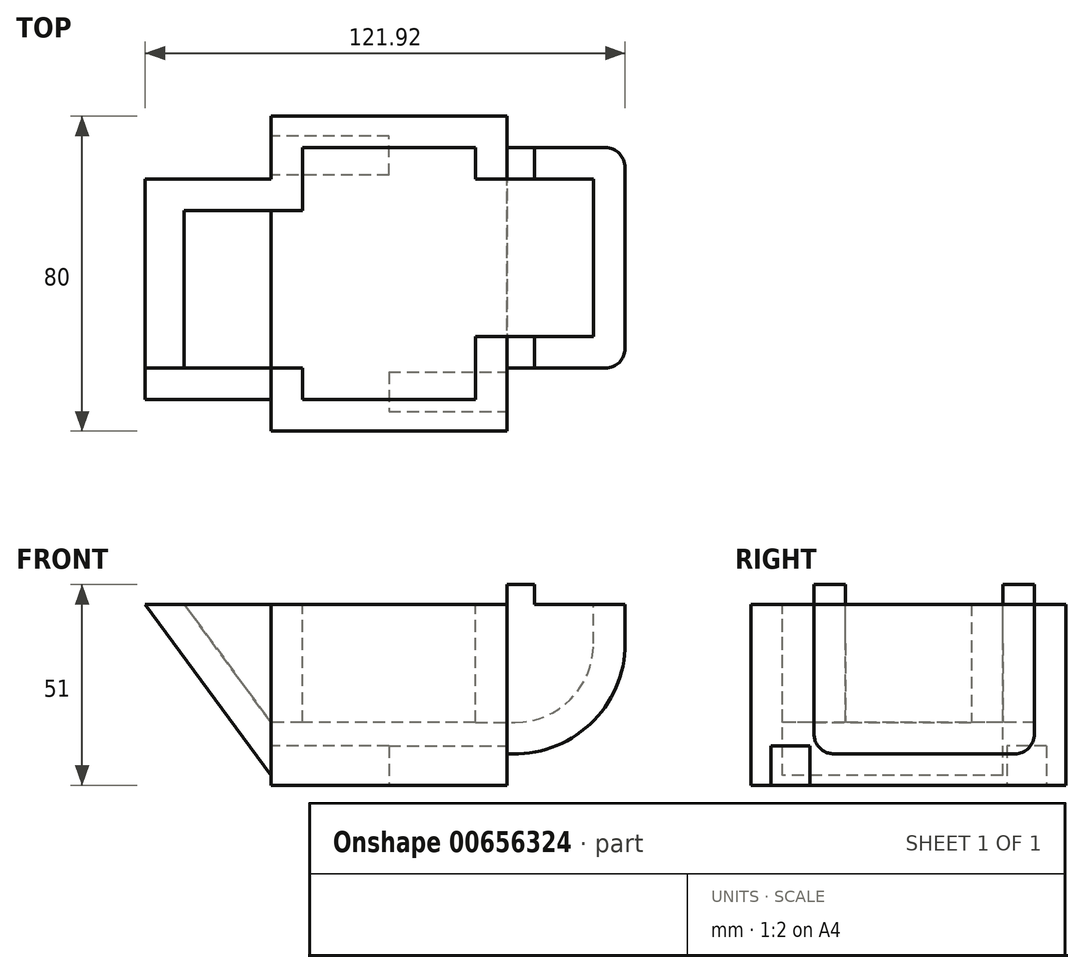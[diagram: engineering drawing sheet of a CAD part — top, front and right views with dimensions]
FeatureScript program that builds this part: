
annotation { "Feature Type Name" : "Feature", "Feature Type Description" : "" }
export const myFeature = defineFeature(function(context is Context, id is Id, definition is map)
    precondition{}
    {
        {
            var Q0;
            Q0=qCreatedBy(makeId("Top.planeOp"),FACE);
            var sketch = newSketch(context, id + "F0", { "sketchPlane" : qUnion([Q0])});
            skLineSegment(sketch, "E0.bottom", {"start": v(30, 40) * mm, "end": v(-30, 40) * mm});
            skLineSegment(sketch, "E0.top", {"start": v(30, -40) * mm, "end": v(-30, -40) * mm});
            skLineSegment(sketch, "E0.left", {"start": v(30, 40) * mm, "end": v(30, -40) * mm});
            skLineSegment(sketch, "E0.right", {"start": v(-30, 40) * mm, "end": v(-30, -40) * mm});
            skPoint(sketch, "E0.middle", {"position": v(0, 0) * mm});
            skSolve(sketch);
        }
        {
            var Q0;
            Q0=makeQuery(id+"F0.imprint","IMPRINT",FACE,{"disambiguationData":[TD([[makeQuery(id+"F0.imprint","IMPRINT",EDGE,{"derivedFrom":sQuery(id+"F0.wireOp",EDGE,"E0.bottom")}),1.0]])]});
            var sketch = newSketch(context, id + "F1", { "sketchPlane" : qUnion([Q0])});
            skCircle(sketch, "E1", {"center": v(0, 0) * mm, "radius": 25 * mm});
            skLineSegment(sketch, "E2.bottom", {"start": v(0, 25) * mm, "end": v(30, 25) * mm});
            skLineSegment(sketch, "E2.top", {"start": v(0, 35) * mm, "end": v(30, 35) * mm});
            skLineSegment(sketch, "E2.left", {"start": v(0, 25) * mm, "end": v(0, 35) * mm});
            skLineSegment(sketch, "E2.right", {"start": v(30, 25) * mm, "end": v(30, 35) * mm});
            skLineSegment(sketch, "E3.bottom", {"start": v(0, 25) * mm, "end": v(-30, 25) * mm});
            skLineSegment(sketch, "E3.top", {"start": v(0, 35) * mm, "end": v(-30, 35) * mm});
            skLineSegment(sketch, "E3.right", {"start": v(-30, 25) * mm, "end": v(-30, 35) * mm});
            skLineSegment(sketch, "E4.MirrorCS", {"start": v(0, -25) * mm, "end": v(30, -25) * mm});
            skLineSegment(sketch, "E5.MirrorCS", {"start": v(30, -25) * mm, "end": v(30, -35) * mm});
            skLineSegment(sketch, "E6.MirrorCS", {"start": v(0, -35) * mm, "end": v(30, -35) * mm});
            skLineSegment(sketch, "E7.MirrorCS", {"start": v(0, -35) * mm, "end": v(-30, -35) * mm});
            skLineSegment(sketch, "E8.MirrorCS", {"start": v(0, -25) * mm, "end": v(-30, -25) * mm});
            skLineSegment(sketch, "E9.MirrorCS", {"start": v(-30, -25) * mm, "end": v(-30, -35) * mm});
            skLineSegment(sketch, "E10", {"start": v(0, -25) * mm, "end": v(0, -35) * mm});
            skSolve(sketch);
        }
        {
            var Q0;
            Q0 = qSketchRegion(id + "F0", true);
            extrude(context, id + "F2", {"entities" : qUnion([Q0]), "depth" : 46 * mm, "offsetDistance" : 25 * mm});
        }
        {
            var Q0;
            Q0=makeQuery(id+"F1.imprint","IMPRINT",FACE,{"disambiguationData":[TD([[makeQuery(id+"F1.imprint","IMPRINT",EDGE,{"derivedFrom":sQuery(id+"F1.wireOp",EDGE,"E3.bottom")}),-1.0]])]});
            var Q1;
            Q1=makeQuery(id+"F1.imprint","IMPRINT",FACE,{"disambiguationData":[TD([[makeQuery(id+"F1.imprint","IMPRINT",EDGE,{"derivedFrom":sQuery(id+"F1.wireOp",EDGE,"E4.MirrorCS")}),-1.0]])]});
            var Q2;
            Q2=makeQuery(id+"F1.imprint","IMPRINT",FACE,{"disambiguationData":[TD([[makeQuery(id+"F1.imprint","IMPRINT",EDGE,{"derivedFrom":sQuery(id+"F1.wireOp",EDGE,"E4.MirrorCS")}),-1.0]])]});
            extrude(context, id + "F3", {"entities" : qUnion([Q0, Q1, Q2]), "operationType" : NewBodyOperationType.REMOVE, "depth" : 10 * mm, "offsetDistance" : 25 * mm});
        }
        {
            var Q0;
            Q0=makeQuery(id+"F2.opExtrude","CAP_FACE",FACE,{"disambiguationData":[OSD([sQuery(id+"F0.wireOp",EDGE,"E0.bottom"),sQuery(id+"F0.wireOp",EDGE,"E0.top"),sQuery(id+"F0.wireOp",EDGE,"E0.left"),sQuery(id+"F0.wireOp",EDGE,"E0.right")])],"isStart":false});
            var sketch = newSketch(context, id + "F4", { "sketchPlane" : qUnion([Q0])});
            skLineSegment(sketch, "E11.bottom", {"start": v(22, 32) * mm, "end": v(-22, 32) * mm});
            skLineSegment(sketch, "E11.top", {"start": v(22, -32) * mm, "end": v(-22, -32) * mm});
            skLineSegment(sketch, "E11.left", {"start": v(22, 32) * mm, "end": v(22, -32) * mm});
            skLineSegment(sketch, "E11.right", {"start": v(-22, 32) * mm, "end": v(-22, -32) * mm});
            skPoint(sketch, "E11.middle", {"position": v(0, 0) * mm});
            skSolve(sketch);
        }
        {
            var Q0;
            Q0=makeQuery(id+"F4.imprint","IMPRINT",FACE,{"disambiguationData":[TD([[makeQuery(id+"F4.imprint","IMPRINT",EDGE,{"derivedFrom":sQuery(id+"F4.wireOp",EDGE,"E11.bottom")}),1.0]])]});
            extrude(context, id + "F5", {"entities" : qUnion([Q0]), "operationType" : NewBodyOperationType.REMOVE, "oppositeDirection" : true, "depth" : 30 * mm, "offsetDistance" : 25 * mm});
        }
        {
            var Q0;
            Q0=makeQuery(id+"F2.opExtrude","CAP_FACE",FACE,{"disambiguationData":[OSD([sQuery(id+"F0.wireOp",EDGE,"E0.bottom"),sQuery(id+"F0.wireOp",EDGE,"E0.top"),sQuery(id+"F0.wireOp",EDGE,"E0.left"),sQuery(id+"F0.wireOp",EDGE,"E0.right")])],"isStart":false});
            var sketch = newSketch(context, id + "F6", { "sketchPlane" : qUnion([Q0])});
            skLineSegment(sketch, "E12.bottom", {"start": v(30, 24) * mm, "end": v(-30, 24) * mm});
            skLineSegment(sketch, "E12.top", {"start": v(30, -24) * mm, "end": v(-30, -24) * mm});
            skLineSegment(sketch, "E12.left", {"start": v(30, 24) * mm, "end": v(30, -24) * mm});
            skLineSegment(sketch, "E12.right", {"start": v(-30, 24) * mm, "end": v(-30, -24) * mm});
            skPoint(sketch, "E12.middle", {"position": v(0, 0) * mm});
            skLineSegment(sketch, "E13.bottom", {"start": v(22, 24) * mm, "end": v(-22, 24) * mm});
            skLineSegment(sketch, "E13.top", {"start": v(22, -24) * mm, "end": v(-22, -24) * mm});
            skLineSegment(sketch, "E13.left", {"start": v(22, 24) * mm, "end": v(22, -24) * mm});
            skLineSegment(sketch, "E13.right", {"start": v(-22, 24) * mm, "end": v(-22, -24) * mm});
            skSolve(sketch);
        }
        {
            var Q0;
            {var subQ0=sQuery(id+"F6.wireOp",EDGE,"E12.right");Q0=makeQuery(id+"F6.imprint","IMPRINT",FACE,{"disambiguationData":[TD([[makeQuery(id+"F6.imprint","IMPRINT",EDGE,{"derivedFrom":subQ0}),1.0]])]});}
            var Q1;
            {var subQ0=sQuery(id+"F6.wireOp",EDGE,"E12.left");Q1=makeQuery(id+"F6.imprint","IMPRINT",FACE,{"disambiguationData":[TD([[makeQuery(id+"F6.imprint","IMPRINT",EDGE,{"derivedFrom":subQ0}),-1.0]])]});}
            var Q2;
            Q2=makeQuery(id+"F5.boolean.opBoolean","COPY",FACE,{"derivedFrom":makeQuery(id+"F5.opExtrude","CAP_FACE",FACE,{"disambiguationData":[OSD([sQuery(id+"F4.wireOp",EDGE,"E11.bottom"),sQuery(id+"F4.wireOp",EDGE,"E11.top"),sQuery(id+"F4.wireOp",EDGE,"E11.left"),sQuery(id+"F4.wireOp",EDGE,"E11.right")])],"isStart":false})});
            extrude(context, id + "F7", {"entities" : qUnion([Q0, Q1]), "operationType" : NewBodyOperationType.REMOVE, "endBound" : BoundingType.UP_TO_SURFACE, "oppositeDirection" : true, "depth" : 25 * mm, "endBoundEntityFace" : qUnion([Q2]), "offsetDistance" : 25 * mm});
        }
        {
            var Q0;
            {var subQ0=sQuery(id+"F6.wireOp",EDGE,"E12.top");Q0=makeQuery(id+"F7.boolean.opBoolean","COPY",FACE,{"derivedFrom":makeQuery(id+"F7.opExtrude","SWEPT_FACE",FACE,{"disambiguationData":[OSD([subQ0]),TDD([makeQuery(id+"F6.imprint","IMPRINT",EDGE,{"disambiguationData":[TD([[makeQuery(id+"F6.imprint","INTERSECT",VERTEX,{"derivedFrom":[makeQuery(id+"F2.opExtrude","CAP_EDGE",EDGE,{"disambiguationData":[OSD([sQuery(id+"F0.wireOp",EDGE,"E0.left")])],"isStart":false}),subQ0,sQuery(id+"F6.wireOp",EDGE,"E12.left")]}),-1.0]])],"derivedFrom":subQ0})])]})});}
            var sketch = newSketch(context, id + "F8", { "sketchPlane" : qUnion([Q0])});
            skLineSegment(sketch, "E14.bottom", {"start": v(-22, 16) * mm, "end": v(-52, 16) * mm});
            skLineSegment(sketch, "E14.top", {"start": v(-22, 46) * mm, "end": v(-52, 46) * mm});
            skLineSegment(sketch, "E14.left", {"start": v(-22, 16) * mm, "end": v(-22, 46) * mm});
            skLineSegment(sketch, "E14.right", {"start": v(-52, 16) * mm, "end": v(-52, 46) * mm});
            skSolve(sketch);
        }
        {
            var Q0;
            {var subQ2=sQuery(id+"F8.wireOp",EDGE,"E14.right");Q0=makeQuery(id+"F8.imprint","IMPRINT",FACE,{"disambiguationData":[TD([[makeQuery(id+"F8.imprint","IMPRINT",EDGE,{"derivedFrom":subQ2}),-1.0]])]});}
            var Q1;
            {var subQ2=sQuery(id+"F8.wireOp",EDGE,"E14.left");Q1=makeQuery(id+"F8.imprint","IMPRINT",FACE,{"disambiguationData":[TD([[makeQuery(id+"F8.imprint","IMPRINT",EDGE,{"derivedFrom":subQ2}),1.0]])]});}
            extrude(context, id + "F9", {"entities" : qUnion([Q0, Q1]), "operationType" : NewBodyOperationType.ADD, "depth" : 8 * mm, "offsetDistance" : 25 * mm});
        }
        {
            var Q0;
            Q0=makeQuery(id+"F9.opExtrude","SWEPT_EDGE",EDGE,{"disambiguationData":[OSD([sQuery(id+"F8.wireOp",EDGE,"E14.bottom"),sQuery(id+"F8.wireOp",EDGE,"E14.right")])]});
            fillet(context, id + "F10", {"entities" : qUnion([Q0]), "radius" : 20 * mm, "tangentPropagation" : true, "allowEdgeOverflow" : false});
        }
        {
            var Q0;
            Q0=makeQuery(id+"F9.opExtrude","CAP_FACE",FACE,{"disambiguationData":[OSD([sQuery(id+"F8.wireOp",EDGE,"E14.bottom"),sQuery(id+"F8.wireOp",EDGE,"E14.top"),sQuery(id+"F8.wireOp",EDGE,"E14.left"),sQuery(id+"F8.wireOp",EDGE,"E14.right")])],"isStart":false});
            var sketch = newSketch(context, id + "F11", { "sketchPlane" : qUnion([Q0])});
            skCircle(sketch, "E15", {"center": v(-32, 36) * mm, "radius": 28 * mm});
            skLineSegment(sketch, "E16", {"start": v(-32, 16) * mm, "end": v(-32, 8) * mm});
            skLineSegment(sketch, "E17", {"start": v(-30, 16) * mm, "end": v(-30, 8) * mm});
            skLineSegment(sketch, "E18", {"start": v(-32, 8) * mm, "end": v(-30, 8) * mm});
            skLineSegment(sketch, "E19", {"start": v(-60, 36) * mm, "end": v(-60, 46) * mm});
            skLineSegment(sketch, "E20", {"start": v(-60, 46) * mm, "end": v(-52, 46) * mm});
            skLineSegment(sketch, "E21", {"start": v(-52, 46) * mm, "end": v(-52, 36) * mm});
            skSolve(sketch);
        }
        {
            var Q0;
            {var subQ0=sQuery(id+"F11.wireOp",EDGE,"E16");Q0=makeQuery(id+"F11.imprint","IMPRINT",FACE,{"disambiguationData":[TD([[makeQuery(id+"F11.imprint","IMPRINT",EDGE,{"derivedFrom":subQ0}),-1.0]])]});}
            var Q1;
            {var subQ0=sQuery(id+"F11.wireOp",EDGE,"E19");Q1=makeQuery(id+"F11.imprint","IMPRINT",FACE,{"disambiguationData":[TD([[makeQuery(id+"F11.imprint","IMPRINT",EDGE,{"derivedFrom":subQ0}),-1.0]])]});}
            var Q2;
            {var subQ0=sQuery(id+"F11.wireOp",EDGE,"E16");Q2=makeQuery(id+"F11.imprint","IMPRINT",FACE,{"disambiguationData":[TD([[makeQuery(id+"F11.imprint","IMPRINT",EDGE,{"derivedFrom":subQ0}),1.0]])]});}
            var Q3;
            Q3=makeQuery(id+"F9.opExtrude","CAP_FACE",FACE,{"disambiguationData":[OSD([sQuery(id+"F8.wireOp",EDGE,"E14.bottom"),sQuery(id+"F8.wireOp",EDGE,"E14.top"),sQuery(id+"F8.wireOp",EDGE,"E14.left"),sQuery(id+"F8.wireOp",EDGE,"E14.right")])],"isStart":true});
            extrude(context, id + "F12", {"entities" : qUnion([Q0, Q1, Q2]), "operationType" : NewBodyOperationType.ADD, "endBound" : BoundingType.UP_TO_SURFACE, "oppositeDirection" : true, "depth" : 25 * mm, "endBoundEntityFace" : qUnion([Q3]), "offsetDistance" : 25 * mm});
        }
        {
            var Q0;
            {var subQ0=sQuery(id+"F8.wireOp",EDGE,"E14.right");var subQ1=sQuery(id+"F8.wireOp",EDGE,"E14.left");var subQ2=sQuery(id+"F8.wireOp",EDGE,"E14.top");var subQ3=sQuery(id+"F8.wireOp",EDGE,"E14.bottom");Q0=makeQuery(id+"F12.boolean.opBoolean","MERGE",FACE,{"derivedFrom":[makeQuery(id+"F9.opExtrude","CAP_FACE",FACE,{"disambiguationData":[OSD([subQ3,subQ2,subQ1,subQ0])],"isStart":false}),makeQuery(id+"F12.opExtrude","CAP_FACE",FACE,{"disambiguationData":[OSD([subQ3,subQ2,subQ1,subQ0,sQuery(id+"F11.wireOp",EDGE,"E15"),sQuery(id+"F11.wireOp",EDGE,"E17"),sQuery(id+"F11.wireOp",EDGE,"E19"),sQuery(id+"F11.wireOp",EDGE,"E20"),sQuery(id+"F11.wireOp",EDGE,"E21")])],"isStart":true})]});}
            var sketch = newSketch(context, id + "F13", { "sketchPlane" : qUnion([Q0])});
            skCircle(sketch, "E22", {"center": v(-32, 36) * mm, "radius": 28 * mm});
            skCircle(sketch, "E23", {"center": v(-32, 36) * mm, "radius": 20 * mm});
            skLineSegment(sketch, "E24", {"start": v(-60, 46) * mm, "end": v(-60, 36) * mm});
            skLineSegment(sketch, "E25", {"start": v(-60, 36) * mm, "end": v(-52, 36) * mm});
            skLineSegment(sketch, "E26", {"start": v(-52, 36) * mm, "end": v(-52, 46) * mm});
            skLineSegment(sketch, "E27", {"start": v(-52, 46) * mm, "end": v(-60, 46) * mm});
            skLineSegment(sketch, "E28", {"start": v(-32, 16) * mm, "end": v(-32, 8) * mm});
            skLineSegment(sketch, "E29", {"start": v(-32, 8) * mm, "end": v(-30, 8) * mm});
            skLineSegment(sketch, "E30", {"start": v(-30, 8) * mm, "end": v(-30, 16) * mm});
            skLineSegment(sketch, "E31", {"start": v(-30, 16) * mm, "end": v(-32, 16) * mm});
            skSolve(sketch);
        }
        {
            var Q0;
            {var subQ0=sQuery(id+"F13.wireOp",EDGE,"E25");Q0=makeQuery(id+"F13.imprint","IMPRINT",FACE,{"disambiguationData":[TD([[makeQuery(id+"F13.imprint","IMPRINT",EDGE,{"derivedFrom":subQ0}),1.0]])]});}
            var Q1;
            {var subQ0=sQuery(id+"F13.wireOp",EDGE,"E24");Q1=makeQuery(id+"F13.imprint","IMPRINT",FACE,{"disambiguationData":[TD([[makeQuery(id+"F13.imprint","IMPRINT",EDGE,{"derivedFrom":subQ0}),-1.0]])]});}
            var Q2;
            {var subQ0=sQuery(id+"F13.wireOp",EDGE,"E25");Q2=makeQuery(id+"F13.imprint","IMPRINT",FACE,{"disambiguationData":[TD([[makeQuery(id+"F13.imprint","IMPRINT",EDGE,{"derivedFrom":subQ0}),-1.0]])]});}
            var Q3;
            {var subQ3=sQuery(id+"F13.wireOp",EDGE,"E28");Q3=makeQuery(id+"F13.imprint","IMPRINT",FACE,{"disambiguationData":[TD([[makeQuery(id+"F13.imprint","IMPRINT",EDGE,{"derivedFrom":subQ3}),1.0]])]});}
            var Q4;
            {var subQ0=sQuery(id+"F6.wireOp",EDGE,"E12.bottom");Q4=makeQuery(id+"F7.boolean.opBoolean","COPY",FACE,{"derivedFrom":makeQuery(id+"F7.opExtrude","SWEPT_FACE",FACE,{"disambiguationData":[OSD([subQ0]),TDD([makeQuery(id+"F6.imprint","IMPRINT",EDGE,{"disambiguationData":[TD([[makeQuery(id+"F6.imprint","INTERSECT",VERTEX,{"derivedFrom":[makeQuery(id+"F2.opExtrude","CAP_EDGE",EDGE,{"disambiguationData":[OSD([sQuery(id+"F0.wireOp",EDGE,"E0.left")])],"isStart":false}),subQ0,sQuery(id+"F6.wireOp",EDGE,"E12.left")]}),-1.0]])],"derivedFrom":subQ0})])]})});}
            extrude(context, id + "F14", {"entities" : qUnion([Q0, Q1, Q2, Q3]), "operationType" : NewBodyOperationType.ADD, "endBound" : BoundingType.UP_TO_SURFACE, "depth" : 25 * mm, "endBoundEntityFace" : qUnion([Q4]), "offsetDistance" : 25 * mm});
        }
        {
            var Q0;
            Q0=makeQuery(id+"F12.opExtrude","CAP_EDGE",EDGE,{"disambiguationData":[OSD([sQuery(id+"F11.wireOp",EDGE,"E15")])],"isStart":false});
            fillet(context, id + "F15", {"entities" : qUnion([Q0]), "radius" : 5 * mm, "tangentPropagation" : true, "allowEdgeOverflow" : false});
        }
        {
            var Q0;
            Q0=makeQuery(id+"F14.opExtrude","CAP_FACE",FACE,{"disambiguationData":[OSD([sQuery(id+"F13.wireOp",EDGE,"E22"),sQuery(id+"F13.wireOp",EDGE,"E23"),sQuery(id+"F13.wireOp",EDGE,"E24"),sQuery(id+"F13.wireOp",EDGE,"E26"),sQuery(id+"F13.wireOp",EDGE,"E27"),sQuery(id+"F13.wireOp",EDGE,"E30"),sQuery(id+"F13.wireOp",EDGE,"E31")])],"isStart":false});
            var sketch = newSketch(context, id + "F16", { "sketchPlane" : qUnion([Q0])});
            skCircle(sketch, "E32", {"center": v(-32, 36) * mm, "radius": 20 * mm});
            skCircle(sketch, "E33", {"center": v(-32, 36) * mm, "radius": 28 * mm});
            skLineSegment(sketch, "E34", {"start": v(-52, 36) * mm, "end": v(-52, 46) * mm});
            skLineSegment(sketch, "E35", {"start": v(-52, 46) * mm, "end": v(-60, 46) * mm});
            skLineSegment(sketch, "E36", {"start": v(-60, 46) * mm, "end": v(-60, 36) * mm});
            skLineSegment(sketch, "E37", {"start": v(-60, 36) * mm, "end": v(-52, 36) * mm});
            skLineSegment(sketch, "E38", {"start": v(-32, 16) * mm, "end": v(-30, 16) * mm});
            skLineSegment(sketch, "E39", {"start": v(-32, 16) * mm, "end": v(-32, 8) * mm});
            skLineSegment(sketch, "E40", {"start": v(-32, 8) * mm, "end": v(-30, 8) * mm});
            skLineSegment(sketch, "E41", {"start": v(-30, 8) * mm, "end": v(-30, 16) * mm});
            skLineSegment(sketch, "E42", {"start": v(-52, 46) * mm, "end": v(-30, 46) * mm});
            skLineSegment(sketch, "E43", {"start": v(-30, 46) * mm, "end": v(-30, 16) * mm});
            skSolve(sketch);
        }
        {
            var Q0;
            {var subQ3=sQuery(id+"F16.wireOp",EDGE,"E40");Q0=makeQuery(id+"F16.imprint","IMPRINT",FACE,{"disambiguationData":[TD([[makeQuery(id+"F16.imprint","IMPRINT",EDGE,{"derivedFrom":subQ3}),1.0]])]});}
            var Q1;
            {var subQ4=sQuery(id+"F16.wireOp",EDGE,"E38");Q1=makeQuery(id+"F16.imprint","IMPRINT",FACE,{"disambiguationData":[TD([[makeQuery(id+"F16.imprint","IMPRINT",EDGE,{"derivedFrom":subQ4}),1.0]])]});}
            var Q2;
            {var subQ0=sQuery(id+"F16.wireOp",EDGE,"E37");Q2=makeQuery(id+"F16.imprint","IMPRINT",FACE,{"disambiguationData":[TD([[makeQuery(id+"F16.imprint","IMPRINT",EDGE,{"derivedFrom":subQ0}),-1.0]])]});}
            var Q3;
            {var subQ0=sQuery(id+"F16.wireOp",EDGE,"E36");Q3=makeQuery(id+"F16.imprint","IMPRINT",FACE,{"disambiguationData":[TD([[makeQuery(id+"F16.imprint","IMPRINT",EDGE,{"derivedFrom":subQ0}),-1.0]])]});}
            var Q4;
            {var subQ4=sQuery(id+"F16.wireOp",EDGE,"E34");Q4=makeQuery(id+"F16.imprint","IMPRINT",FACE,{"disambiguationData":[TD([[makeQuery(id+"F16.imprint","IMPRINT",EDGE,{"derivedFrom":subQ4}),1.0]])]});}
            var Q5;
            {var subQ0=sQuery(id+"F16.wireOp",EDGE,"E38");Q5=makeQuery(id+"F16.imprint","IMPRINT",FACE,{"disambiguationData":[TD([[makeQuery(id+"F16.imprint","IMPRINT",EDGE,{"derivedFrom":subQ0}),-1.0]])]});}
            var Q6;
            {var subQ0=sQuery(id+"F16.wireOp",EDGE,"E43");var subQ1=sQuery(id+"F16.wireOp",EDGE,"E42");var subQ2=makeQuery(id+"F16.imprint","INTERSECT",VERTEX,{"derivedFrom":[subQ1,subQ0]});Q6=makeQuery(id+"F16.imprint","IMPRINT",FACE,{"disambiguationData":[TD([[makeQuery(id+"F16.imprint","IMPRINT",EDGE,{"disambiguationData":[TD([[subQ2,1.0]])],"derivedFrom":subQ1}),-1.0]])]});}
            var Q7;
            {var subQ0=sQuery(id+"F16.wireOp",EDGE,"E34");Q7=makeQuery(id+"F16.imprint","IMPRINT",FACE,{"disambiguationData":[TD([[makeQuery(id+"F16.imprint","IMPRINT",EDGE,{"derivedFrom":subQ0}),-1.0]])]});}
            extrude(context, id + "F17", {"entities" : qUnion([Q0, Q1, Q2, Q3, Q4, Q5, Q6, Q7]), "operationType" : NewBodyOperationType.ADD, "depth" : 8 * mm, "offsetDistance" : 25 * mm});
        }
        {
            var Q0;
            Q0=makeQuery(id+"F17.opExtrude","CAP_EDGE",EDGE,{"disambiguationData":[OSD([sQuery(id+"F16.wireOp",EDGE,"E33")])],"isStart":false});
            fillet(context, id + "F18", {"entities" : qUnion([Q0]), "radius" : 5 * mm, "tangentPropagation" : true, "allowEdgeOverflow" : false});
        }
        {
            var Q0;
            {var subQ0=sQuery(id+"F0.wireOp",EDGE,"E0.right");var subQ4=sQuery(id+"F0.wireOp",EDGE,"E0.left");var subQ6=sQuery(id+"F0.wireOp",EDGE,"E0.top");var subQ19=sQuery(id+"F0.wireOp",EDGE,"E0.bottom");var subQ20=makeQuery(id+"F2.opExtrude","CAP_FACE",FACE,{"disambiguationData":[OSD([subQ19,subQ6,subQ4,subQ0])],"isStart":false});Q0=makeQuery(id+"F17.boolean.opBoolean","MERGE",FACE,{"derivedFrom":[makeQuery(id+"F7.boolean.opBoolean","SPLIT",FACE,{"disambiguationData":[TD([makeQuery(id+"F2.opExtrude","SWEPT_FACE",FACE,{"disambiguationData":[OSD([subQ19])]})])],"derivedFrom":subQ20}),makeQuery(id+"F14.boolean.opBoolean","MERGE",FACE,{"derivedFrom":[makeQuery(id+"F12.boolean.opBoolean","MERGE",FACE,{"derivedFrom":[makeQuery(id+"F9.boolean.opBoolean","MERGE",FACE,{"derivedFrom":[makeQuery(id+"F7.boolean.opBoolean","SPLIT",FACE,{"disambiguationData":[TD([makeQuery(id+"F2.opExtrude","SWEPT_FACE",FACE,{"disambiguationData":[OSD([subQ6])]})])],"derivedFrom":subQ20}),makeQuery(id+"F9.opExtrude","SWEPT_FACE",FACE,{"disambiguationData":[OSD([sQuery(id+"F8.wireOp",EDGE,"E14.top")])]})]}),makeQuery(id+"F12.opExtrude","SWEPT_FACE",FACE,{"disambiguationData":[OSD([sQuery(id+"F11.wireOp",EDGE,"E20")])]})]}),makeQuery(id+"F14.opExtrude","SWEPT_FACE",FACE,{"disambiguationData":[OSD([sQuery(id+"F13.wireOp",EDGE,"E27")])]})]}),makeQuery(id+"F17.opExtrude","SWEPT_FACE",FACE,{"disambiguationData":[OSD([sQuery(id+"F16.wireOp",EDGE,"E35"),sQuery(id+"F16.wireOp",EDGE,"E42")])]})]});}
            var sketch = newSketch(context, id + "F19", { "sketchPlane" : qUnion([Q0])});
            skLineSegment(sketch, "E44.bottom", {"start": v(30, 32) * mm, "end": v(37, 32) * mm});
            skLineSegment(sketch, "E44.top", {"start": v(30, 24) * mm, "end": v(37, 24) * mm});
            skLineSegment(sketch, "E44.left", {"start": v(30, 32) * mm, "end": v(30, 24) * mm});
            skLineSegment(sketch, "E44.right", {"start": v(37, 32) * mm, "end": v(37, 24) * mm});
            skLineSegment(sketch, "E45.bottom", {"start": v(30, -24) * mm, "end": v(37, -24) * mm});
            skLineSegment(sketch, "E45.top", {"start": v(30, -16) * mm, "end": v(37, -16) * mm});
            skLineSegment(sketch, "E45.left", {"start": v(30, -24) * mm, "end": v(30, -16) * mm});
            skLineSegment(sketch, "E45.right", {"start": v(37, -24) * mm, "end": v(37, -16) * mm});
            skSolve(sketch);
        }
        {
            var Q0;
            Q0=makeQuery(id+"F19.imprint","IMPRINT",FACE,{"disambiguationData":[TD([[makeQuery(id+"F19.imprint","IMPRINT",EDGE,{"derivedFrom":sQuery(id+"F19.wireOp",EDGE,"E44.bottom")}),-1.0]])]});
            var Q1;
            Q1=makeQuery(id+"F19.imprint","IMPRINT",FACE,{"disambiguationData":[TD([[makeQuery(id+"F19.imprint","IMPRINT",EDGE,{"derivedFrom":sQuery(id+"F19.wireOp",EDGE,"E45.bottom")}),1.0]])]});
            extrude(context, id + "F20", {"entities" : qUnion([Q0, Q1]), "operationType" : NewBodyOperationType.ADD, "depth" : 5 * mm, "offsetDistance" : 25 * mm});
        }
        {
            var Q0;
            {var subQ0=sQuery(id+"F6.wireOp",EDGE,"E12.bottom");Q0=makeQuery(id+"F7.boolean.opBoolean","COPY",FACE,{"derivedFrom":makeQuery(id+"F7.opExtrude","SWEPT_FACE",FACE,{"disambiguationData":[OSD([subQ0]),TDD([makeQuery(id+"F6.imprint","IMPRINT",EDGE,{"disambiguationData":[TD([[makeQuery(id+"F6.imprint","INTERSECT",VERTEX,{"derivedFrom":[makeQuery(id+"F2.opExtrude","CAP_EDGE",EDGE,{"disambiguationData":[OSD([sQuery(id+"F0.wireOp",EDGE,"E0.right")])],"isStart":false}),subQ0,sQuery(id+"F6.wireOp",EDGE,"E12.right")]}),1.0]])],"derivedFrom":subQ0})])]})});}
            var sketch = newSketch(context, id + "F21", { "sketchPlane" : qUnion([Q0])});
            skLineSegment(sketch, "E46.bottom", {"start": v(-22, 46) * mm, "end": v(-52, 46) * mm});
            skLineSegment(sketch, "E46.top", {"start": v(-22, 16) * mm, "end": v(-52, 16) * mm});
            skLineSegment(sketch, "E46.left", {"start": v(-22, 46) * mm, "end": v(-22, 16) * mm});
            skLineSegment(sketch, "E46.right", {"start": v(-52, 46) * mm, "end": v(-52, 16) * mm});
            skSolve(sketch);
        }
        {
            var Q0;
            {var subQ2=sQuery(id+"F21.wireOp",EDGE,"E46.right");Q0=makeQuery(id+"F21.imprint","IMPRINT",FACE,{"disambiguationData":[TD([[makeQuery(id+"F21.imprint","IMPRINT",EDGE,{"derivedFrom":subQ2}),1.0]])]});}
            var Q1;
            {var subQ2=sQuery(id+"F21.wireOp",EDGE,"E46.left");Q1=makeQuery(id+"F21.imprint","IMPRINT",FACE,{"disambiguationData":[TD([[makeQuery(id+"F21.imprint","IMPRINT",EDGE,{"derivedFrom":subQ2}),1.0]])]});}
            extrude(context, id + "F22", {"entities" : qUnion([Q0, Q1]), "operationType" : NewBodyOperationType.ADD, "depth" : 8 * mm, "offsetDistance" : 25 * mm});
        }
        {
            var Q0;
            Q0=makeQuery(id+"F22.opExtrude","SWEPT_EDGE",EDGE,{"disambiguationData":[OSD([sQuery(id+"F21.wireOp",EDGE,"E46.top"),sQuery(id+"F21.wireOp",EDGE,"E46.right")])]});
            chamfer(context, id + "F23", {"entities" : qUnion([Q0]), "chamferType" : ChamferType.TWO_OFFSETS, "width1" : 22 * mm, "oppositeDirection" : false, "width2" : 30 * mm, "tangentPropagation" : true});
        }
        {
            var Q0;
            Q0=makeQuery(id+"F22.opExtrude","CAP_FACE",FACE,{"disambiguationData":[OSD([sQuery(id+"F21.wireOp",EDGE,"E46.bottom"),sQuery(id+"F21.wireOp",EDGE,"E46.top"),sQuery(id+"F21.wireOp",EDGE,"E46.left"),sQuery(id+"F21.wireOp",EDGE,"E46.right")])],"isStart":false});
            var sketch = newSketch(context, id + "F24", { "sketchPlane" : qUnion([Q0])});
            skLineSegment(sketch, "E47", {"start": v(-52, 46) * mm, "end": v(-30, 16) * mm});
            skLineSegment(sketch, "E48", {"start": v(-30, 16) * mm, "end": v(-30, 46) * mm});
            skLineSegment(sketch, "E49", {"start": v(-30, 46) * mm, "end": v(-52, 46) * mm});
            skLineSegment(sketch, "E50", {"start": v(-61.92, 46) * mm, "end": v(-30, 2.47) * mm});
            skLineSegment(sketch, "E51", {"start": v(-30, 2.47) * mm, "end": v(-30, 16) * mm});
            skLineSegment(sketch, "E52", {"start": v(-52, 46) * mm, "end": v(-61.92, 46) * mm});
            skSolve(sketch);
        }
        {
            var Q0;
            Q0=makeQuery(id+"F24.imprint","IMPRINT",FACE,{"disambiguationData":[TD([[makeQuery(id+"F24.imprint","IMPRINT",EDGE,{"derivedFrom":sQuery(id+"F24.wireOp",EDGE,"E47")}),-1.0]])]});
            extrude(context, id + "F25", {"entities" : qUnion([Q0]), "operationType" : NewBodyOperationType.ADD, "oppositeDirection" : true, "depth" : 8 * mm, "offsetDistance" : 25 * mm});
        }
        {
            var Q0;
            Q0=makeQuery(id+"F25.boolean.opBoolean","MERGE",FACE,{"derivedFrom":[makeQuery(id+"F22.opExtrude","CAP_FACE",FACE,{"disambiguationData":[OSD([sQuery(id+"F21.wireOp",EDGE,"E46.bottom"),sQuery(id+"F21.wireOp",EDGE,"E46.top"),sQuery(id+"F21.wireOp",EDGE,"E46.left"),sQuery(id+"F21.wireOp",EDGE,"E46.right")])],"isStart":false}),makeQuery(id+"F25.opExtrude","CAP_FACE",FACE,{"disambiguationData":[OSD([sQuery(id+"F24.wireOp",EDGE,"E47"),sQuery(id+"F24.wireOp",EDGE,"E50"),sQuery(id+"F24.wireOp",EDGE,"E51"),sQuery(id+"F24.wireOp",EDGE,"E52")])],"isStart":true})]});
            var sketch = newSketch(context, id + "F26", { "sketchPlane" : qUnion([Q0])});
            skLineSegment(sketch, "E53", {"start": v(-30, 2.47) * mm, "end": v(-61.92, 46) * mm});
            skLineSegment(sketch, "E54", {"start": v(-61.92, 46) * mm, "end": v(-52, 46) * mm});
            skLineSegment(sketch, "E55", {"start": v(-52, 46) * mm, "end": v(-30, 16) * mm});
            skLineSegment(sketch, "E56", {"start": v(-30, 16) * mm, "end": v(-30, 2.47) * mm});
            skSolve(sketch);
        }
        {
            var Q0;
            Q0=makeQuery(id+"F26.imprint","IMPRINT",FACE,{"disambiguationData":[TD([[makeQuery(id+"F26.imprint","IMPRINT",EDGE,{"derivedFrom":sQuery(id+"F26.wireOp",EDGE,"E53")}),1.0]])]});
            var Q1;
            {var subQ0=sQuery(id+"F6.wireOp",EDGE,"E12.top");Q1=makeQuery(id+"F7.boolean.opBoolean","COPY",FACE,{"derivedFrom":makeQuery(id+"F7.opExtrude","SWEPT_FACE",FACE,{"disambiguationData":[OSD([subQ0]),TDD([makeQuery(id+"F6.imprint","IMPRINT",EDGE,{"disambiguationData":[TD([[makeQuery(id+"F6.imprint","INTERSECT",VERTEX,{"derivedFrom":[makeQuery(id+"F2.opExtrude","CAP_EDGE",EDGE,{"disambiguationData":[OSD([sQuery(id+"F0.wireOp",EDGE,"E0.right")])],"isStart":false}),subQ0,sQuery(id+"F6.wireOp",EDGE,"E12.right")]}),1.0]])],"derivedFrom":subQ0})])]})});}
            extrude(context, id + "F27", {"entities" : qUnion([Q0]), "operationType" : NewBodyOperationType.ADD, "endBound" : BoundingType.UP_TO_SURFACE, "depth" : 25 * mm, "endBoundEntityFace" : qUnion([Q1]), "offsetDistance" : 25 * mm});
        }
        {
            var Q0;
            Q0=makeQuery(id+"F27.opExtrude","CAP_FACE",FACE,{"disambiguationData":[OSD([sQuery(id+"F26.wireOp",EDGE,"E53"),sQuery(id+"F26.wireOp",EDGE,"E54"),sQuery(id+"F26.wireOp",EDGE,"E55"),sQuery(id+"F26.wireOp",EDGE,"E56")])],"isStart":false});
            var sketch = newSketch(context, id + "F28", { "sketchPlane" : qUnion([Q0])});
            skLineSegment(sketch, "E57", {"start": v(-30, 2.47) * mm, "end": v(-30, 45.88) * mm});
            skLineSegment(sketch, "E58", {"start": v(-30, 45.88) * mm, "end": v(-61.92, 46) * mm});
            skLineSegment(sketch, "E59", {"start": v(-61.92, 46) * mm, "end": v(-30, 2.47) * mm});
            skSolve(sketch);
        }
        {
            var Q0;
            {var subQ0=sQuery(id+"F28.wireOp",EDGE,"E57");var subQ4=sQuery(id+"F28.wireOp",EDGE,"E58");var subQ5=makeQuery(id+"F28.imprint","INTERSECT",VERTEX,{"derivedFrom":[subQ0,subQ4]});Q0=makeQuery(id+"F28.imprint","IMPRINT",FACE,{"disambiguationData":[TD([[makeQuery(id+"F28.imprint","IMPRINT",EDGE,{"disambiguationData":[TD([[subQ5,1.0]])],"derivedFrom":subQ0}),1.0]])]});}
            var Q1;
            {var subQ5=sQuery(id+"F28.wireOp",EDGE,"E59");Q1=makeQuery(id+"F28.imprint","IMPRINT",FACE,{"disambiguationData":[TD([[makeQuery(id+"F28.imprint","IMPRINT",EDGE,{"derivedFrom":subQ5}),-1.0]])]});}
            extrude(context, id + "F29", {"entities" : qUnion([Q0, Q1]), "operationType" : NewBodyOperationType.ADD, "depth" : 8 * mm, "offsetDistance" : 25 * mm});
        }
    });
